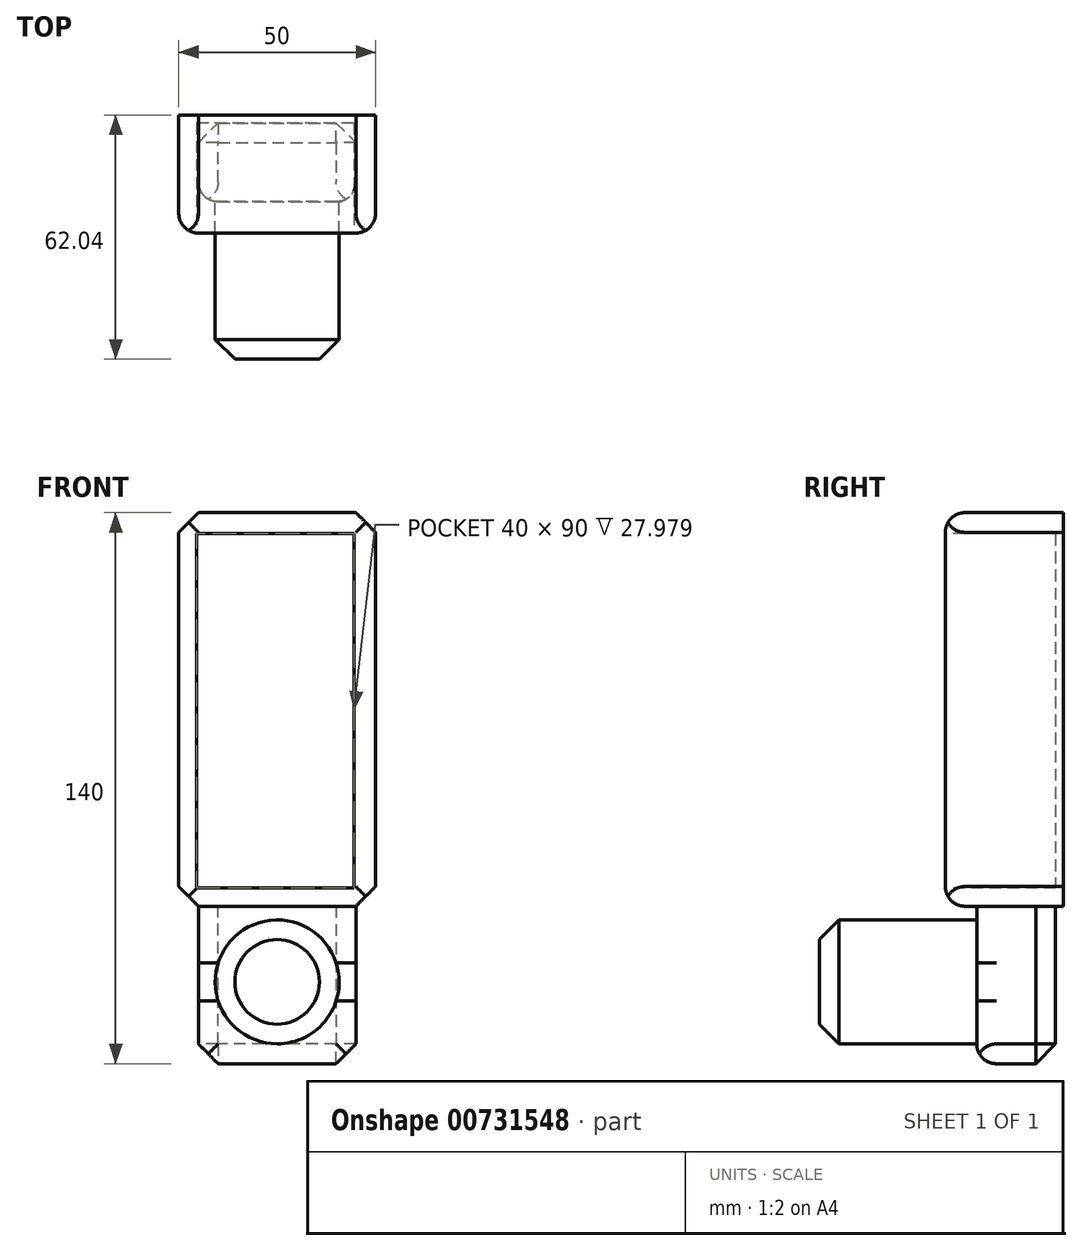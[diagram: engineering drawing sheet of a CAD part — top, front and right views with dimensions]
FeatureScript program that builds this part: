
annotation { "Feature Type Name" : "Feature", "Feature Type Description" : "" }
export const myFeature = defineFeature(function(context is Context, id is Id, definition is map)
    precondition{}
    {
        {
            var Q0;
            Q0=qCreatedBy(makeId("Front.planeOp"),FACE);
            var sketch = newSketch(context, id + "F0", { "sketchPlane" : qUnion([Q0])});
            skLineSegment(sketch, "E0.bottom", {"start": v(25, 50) * mm, "end": v(-25, 50) * mm});
            skLineSegment(sketch, "E0.top", {"start": v(25, -50) * mm, "end": v(-25, -50) * mm});
            skLineSegment(sketch, "E0.left", {"start": v(25, 50) * mm, "end": v(25, -50) * mm});
            skLineSegment(sketch, "E0.right", {"start": v(-25, 50) * mm, "end": v(-25, -50) * mm});
            skPoint(sketch, "E0.middle", {"position": v(0, 0) * mm});
            skSolve(sketch);
        }
        {
            var Q0;
            Q0=makeQuery(id+"F0.imprint","IMPRINT",FACE,{"disambiguationData":[TD([[makeQuery(id+"F0.imprint","IMPRINT",EDGE,{"derivedFrom":sQuery(id+"F0.wireOp",EDGE,"E0.bottom")}),1.0]])]});
            var sketch = newSketch(context, id + "F1", { "sketchPlane" : qUnion([Q0])});
            skSolve(sketch);
        }
        {
            var Q0;
            Q0 = qSketchRegion(id + "F1", true);
            var Q1;
            Q1=makeQuery(id+"F1.imprint","IMPRINT",FACE,{"disambiguationData":[TD([[makeQuery(id+"F1.imprint","IMPRINT",EDGE,{"derivedFrom":makeQuery(id+"F0.imprint","IMPRINT",EDGE,{"derivedFrom":sQuery(id+"F0.wireOp",EDGE,"E0.bottom")})}),1.0]])]});
            extrude(context, id + "F2", {"entities" : qUnion([Q0, Q1]), "depth" : 30 * mm, "offsetDistance" : 25 * mm});
        }
        {
            var Q0;
            Q0=makeQuery(id+"F2.opExtrude","CAP_FACE",FACE,{"disambiguationData":[OSD([sQuery(id+"F0.wireOp",EDGE,"E0.bottom"),sQuery(id+"F0.wireOp",EDGE,"E0.top"),sQuery(id+"F0.wireOp",EDGE,"E0.left"),sQuery(id+"F0.wireOp",EDGE,"E0.right")])],"isStart":false});
            var sketch = newSketch(context, id + "F3", { "sketchPlane" : qUnion([Q0])});
            skSolve(sketch);
        }
        {
            var Q0;
            Q0=makeQuery(id+"F3.imprint","IMPRINT",FACE,{"disambiguationData":[TD([[makeQuery(id+"F3.imprint","IMPRINT",EDGE,{"derivedFrom":makeQuery(id+"F2.opExtrude","CAP_EDGE",EDGE,{"disambiguationData":[OSD([sQuery(id+"F0.wireOp",EDGE,"E0.bottom")])],"isStart":false})}),1.0]])]});
            var sketch = newSketch(context, id + "F4", { "sketchPlane" : qUnion([Q0])});
            skLineSegment(sketch, "E1.bottom", {"start": v(-20.46, 44.7) * mm, "end": v(19.54, 44.7) * mm});
            skLineSegment(sketch, "E1.top", {"start": v(-20.46, -45.3) * mm, "end": v(19.54, -45.3) * mm});
            skLineSegment(sketch, "E1.left", {"start": v(-20.46, 44.7) * mm, "end": v(-20.46, -45.3) * mm});
            skLineSegment(sketch, "E1.right", {"start": v(19.54, 44.7) * mm, "end": v(19.54, -45.3) * mm});
            skSolve(sketch);
        }
        {
            var Q0;
            Q0 = qSketchRegion(id + "F4", true);
            extrude(context, id + "F5", {"entities" : qUnion([Q0]), "operationType" : NewBodyOperationType.REMOVE, "oppositeDirection" : true, "depth" : 28 * mm, "offsetDistance" : 25 * mm});
        }
        {
            var Q0;
            Q0=makeQuery(id+"F2.opExtrude","SWEPT_EDGE",EDGE,{"disambiguationData":[OSD([sQuery(id+"F0.wireOp",EDGE,"E0.bottom"),sQuery(id+"F0.wireOp",EDGE,"E0.left")])]});
            var Q1;
            Q1=makeQuery(id+"F2.opExtrude","SWEPT_EDGE",EDGE,{"disambiguationData":[OSD([sQuery(id+"F0.wireOp",EDGE,"E0.bottom"),sQuery(id+"F0.wireOp",EDGE,"E0.right")])]});
            var Q2;
            Q2=makeQuery(id+"F2.opExtrude","SWEPT_EDGE",EDGE,{"disambiguationData":[OSD([sQuery(id+"F0.wireOp",EDGE,"E0.top"),sQuery(id+"F0.wireOp",EDGE,"E0.right")])]});
            var Q3;
            Q3=makeQuery(id+"F2.opExtrude","SWEPT_EDGE",EDGE,{"disambiguationData":[OSD([sQuery(id+"F0.wireOp",EDGE,"E0.top"),sQuery(id+"F0.wireOp",EDGE,"E0.left")])]});
            chamfer(context, id + "F6", {"entities" : qUnion([Q0, Q1, Q2, Q3]), "width" : 5 * mm, "tangentPropagation" : true});
        }
        {
            var Q0;
            Q0=makeQuery(id+"F2.opExtrude","CAP_EDGE",EDGE,{"disambiguationData":[OSD([sQuery(id+"F0.wireOp",EDGE,"E0.right")])],"isStart":false});
            var Q1;
            Q1=makeQuery(id+"F2.opExtrude","CAP_EDGE",EDGE,{"disambiguationData":[OSD([sQuery(id+"F0.wireOp",EDGE,"E0.bottom")])],"isStart":false});
            var Q2;
            Q2=makeQuery(id+"F2.opExtrude","CAP_EDGE",EDGE,{"disambiguationData":[OSD([sQuery(id+"F0.wireOp",EDGE,"E0.left")])],"isStart":false});
            var Q3;
            Q3=makeQuery(id+"F2.opExtrude","CAP_EDGE",EDGE,{"disambiguationData":[OSD([sQuery(id+"F0.wireOp",EDGE,"E0.top")])],"isStart":false});
            fillet(context, id + "F7", {"entities" : qUnion([Q0, Q1, Q2, Q3]), "radius" : 5 * mm, "tangentPropagation" : true, "allowEdgeOverflow" : false});
        }
        {
            var Q0;
            Q0=makeQuery(id+"F2.opExtrude","SWEPT_FACE",FACE,{"disambiguationData":[OSD([sQuery(id+"F0.wireOp",EDGE,"E0.top")])]});
            var sketch = newSketch(context, id + "F8", { "sketchPlane" : qUnion([Q0])});
            skLineSegment(sketch, "E2.bottom", {"start": v(-20, 22.04) * mm, "end": v(20, 22.04) * mm});
            skLineSegment(sketch, "E2.top", {"start": v(-20, 2.04) * mm, "end": v(20, 2.04) * mm});
            skLineSegment(sketch, "E2.left", {"start": v(-20, 22.04) * mm, "end": v(-20, 2.04) * mm});
            skLineSegment(sketch, "E2.right", {"start": v(20, 22.04) * mm, "end": v(20, 2.04) * mm});
            skSolve(sketch);
        }
        {
            var Q0;
            Q0 = qSketchRegion(id + "F8", true);
            extrude(context, id + "F9", {"entities" : qUnion([Q0]), "operationType" : NewBodyOperationType.ADD, "depth" : 40 * mm, "offsetDistance" : 25 * mm});
        }
        {
            var Q0;
            Q0=makeQuery(id+"F9.opExtrude","SWEPT_FACE",FACE,{"disambiguationData":[OSD([sQuery(id+"F8.wireOp",EDGE,"E2.bottom")])]});
            var sketch = newSketch(context, id + "F10", { "sketchPlane" : qUnion([Q0])});
            skCircle(sketch, "E3", {"center": v(0, -69.22) * mm, "radius": 15.75 * mm});
            skSolve(sketch);
        }
        {
            var Q0;
            Q0 = qSketchRegion(id + "F10", true);
            extrude(context, id + "F11", {"entities" : qUnion([Q0]), "operationType" : NewBodyOperationType.ADD, "depth" : 40 * mm, "offsetDistance" : 25 * mm});
        }
        {
            var Q0;
            Q0=makeQuery(id+"F9.opExtrude","SWEPT_EDGE",EDGE,{"disambiguationData":[OSD([sQuery(id+"F0.wireOp",EDGE,"E0.top"),sQuery(id+"F0.wireOp",EDGE,"E0.right"),sQuery(id+"F8.wireOp",EDGE,"E2.bottom"),sQuery(id+"F8.wireOp",EDGE,"E2.left")])]});
            var Q1;
            Q1=makeQuery(id+"F9.opExtrude","SWEPT_EDGE",EDGE,{"disambiguationData":[OSD([sQuery(id+"F0.wireOp",EDGE,"E0.top"),sQuery(id+"F0.wireOp",EDGE,"E0.left"),sQuery(id+"F8.wireOp",EDGE,"E2.bottom"),sQuery(id+"F8.wireOp",EDGE,"E2.right")])]});
            var Q2;
            Q2=makeQuery(id+"F9.opExtrude","CAP_EDGE",EDGE,{"disambiguationData":[OSD([sQuery(id+"F8.wireOp",EDGE,"E2.bottom")])],"isStart":false});
            fillet(context, id + "F12", {"entities" : qUnion([Q0, Q1, Q2]), "radius" : 5 * mm, "tangentPropagation" : true, "allowEdgeOverflow" : false});
        }
        {
            var Q0;
            Q0=makeQuery(id+"F9.opExtrude","CAP_EDGE",EDGE,{"disambiguationData":[OSD([sQuery(id+"F8.wireOp",EDGE,"E2.left")])],"isStart":false});
            var Q1;
            Q1=makeQuery(id+"F9.opExtrude","CAP_FACE",FACE,{"disambiguationData":[OSD([sQuery(id+"F8.wireOp",EDGE,"E2.bottom"),sQuery(id+"F8.wireOp",EDGE,"E2.top"),sQuery(id+"F8.wireOp",EDGE,"E2.left"),sQuery(id+"F8.wireOp",EDGE,"E2.right")])],"isStart":false});
            var Q2;
            Q2=makeQuery(id+"F9.opExtrude","SWEPT_EDGE",EDGE,{"disambiguationData":[OSD([sQuery(id+"F0.wireOp",EDGE,"E0.top"),sQuery(id+"F0.wireOp",EDGE,"E0.left"),sQuery(id+"F8.wireOp",EDGE,"E2.top"),sQuery(id+"F8.wireOp",EDGE,"E2.right")])]});
            var Q3;
            Q3=makeQuery(id+"F9.opExtrude","SWEPT_EDGE",EDGE,{"disambiguationData":[OSD([sQuery(id+"F0.wireOp",EDGE,"E0.top"),sQuery(id+"F0.wireOp",EDGE,"E0.right"),sQuery(id+"F8.wireOp",EDGE,"E2.top"),sQuery(id+"F8.wireOp",EDGE,"E2.left")])]});
            var Q4;
            Q4=makeQuery(id+"F11.opExtrude","CAP_FACE",FACE,{"disambiguationData":[OSD([sQuery(id+"F10.wireOp",EDGE,"E3")])],"isStart":false});
            chamfer(context, id + "F13", {"entities" : qUnion([Q0, Q1, Q2, Q3, Q4]), "width" : 5 * mm, "tangentPropagation" : true});
        }
    });
